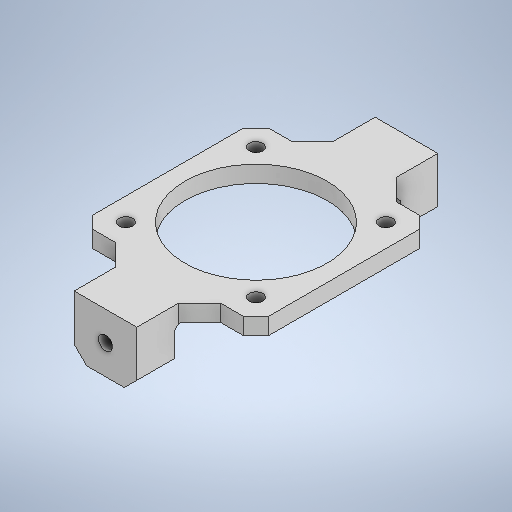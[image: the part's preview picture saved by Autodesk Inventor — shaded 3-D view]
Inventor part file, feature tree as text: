
AUTODESK INVENTOR PART (.ipt)
format: ipt  version: 2025 (Build 290162010, 162A)  size: 329,216 bytes
history: native  units: in
note: dims shown in document units (in); Inventor stores cm internally (conversion verified against a paired STEP export)
features: extrude x3, chamfer x3, sketch x3
ambient origin geometry x8: Origin, YZ Plane, XZ Plane, XY Plane, X Axis, Y Axis, Z Axis, Center Point
bodies: Body1 (feature_tree)
feature tree (9):
  extrude  "Extrusion24"  Depth=1.6535in
  extrude  "Extrusion25"  Depth=1.2248in
  extrude  "Extrusion26"  Depth=0.5906in
  chamfer  "Fasen5"  Distance=0.5906in
  chamfer  "Fasen6"  Distance=0.5315in
  chamfer  "Fasen7"  Distance=0.3543in
  sketch  "Skizze24"  dims[d120=1.6535in d121=1.3386in]
  sketch  "Skizze25"  dims[d122=0.128in d123=1.2248in]
  sketch  "Skizze26"  dims[d124=0.1575in d125=0.0in d126=0.5906in d127=0.5906in d128=0.5315in d129=0.3543in d130=0.3543in d131=0.3937in d132=0.0in d133=0.1319in d134=0.0in d135=0.0in d142=0.1181in d143=0.0787in d144=45.0deg d145=0.0492in d146=0.0787in d147=45.0deg d148=0.1969in d149=0.0787in d150=45.0deg d37=0.0197in d38=0.0344in d39=0.0197in d40=0.0344in d41=0.0197in d42=0.0344in]
